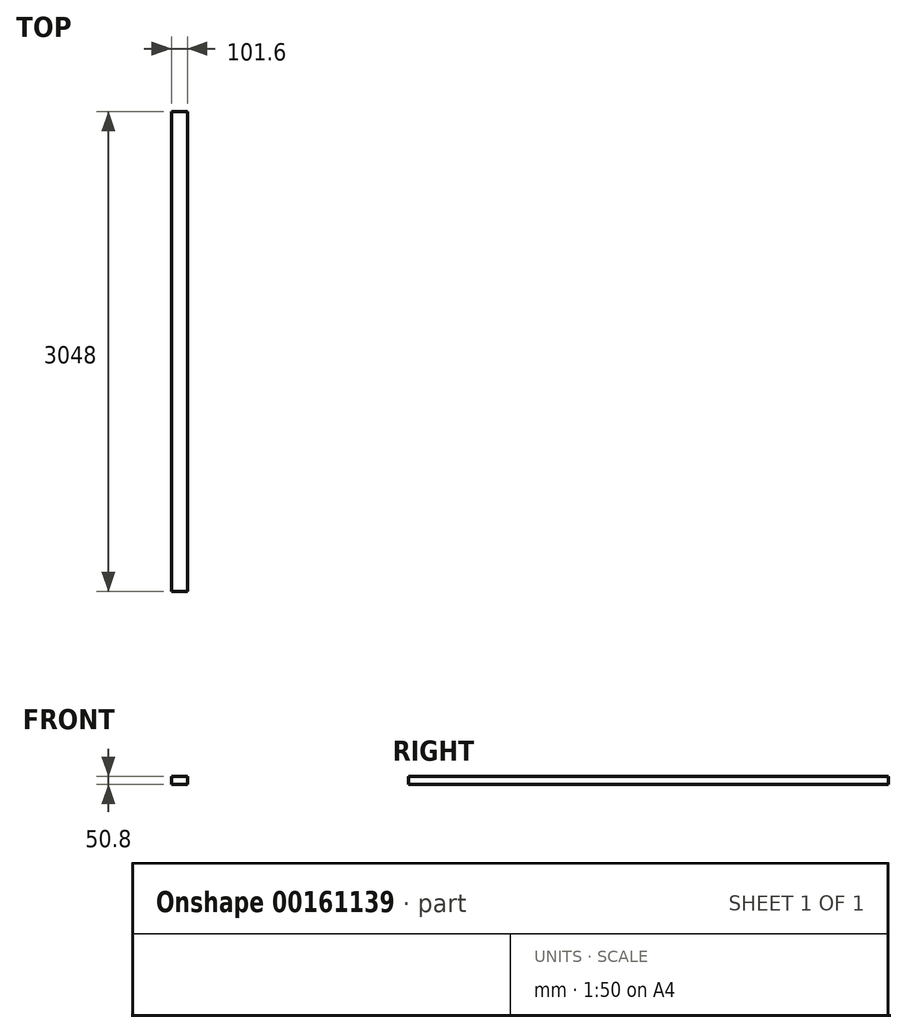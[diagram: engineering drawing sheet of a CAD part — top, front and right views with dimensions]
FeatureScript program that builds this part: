
annotation { "Feature Type Name" : "Feature", "Feature Type Description" : "" }
export const myFeature = defineFeature(function(context is Context, id is Id, definition is map)
    precondition{}
    {
        {
            var Q0;
            Q0=qCreatedBy(makeId("Front.planeOp"),FACE);
            var sketch = newSketch(context, id + "F0", { "sketchPlane" : qUnion([Q0])});
            skLineSegment(sketch, "E0.bottom", {"start": v(0, 0) * mm, "end": v(101.6, 0) * mm});
            skLineSegment(sketch, "E0.top", {"start": v(0, 50.8) * mm, "end": v(101.6, 50.8) * mm});
            skLineSegment(sketch, "E0.left", {"start": v(0, 0) * mm, "end": v(0, 50.8) * mm});
            skLineSegment(sketch, "E0.right", {"start": v(101.6, 0) * mm, "end": v(101.6, 50.8) * mm});
            skSolve(sketch);
        }
        {
            var Q0;
            Q0=qSketchRegion(id+"F0",true);
            extrude(context, id + "F1", {"entities" : qUnion([Q0]), "depth" : 3048 * mm});
        }
    });
